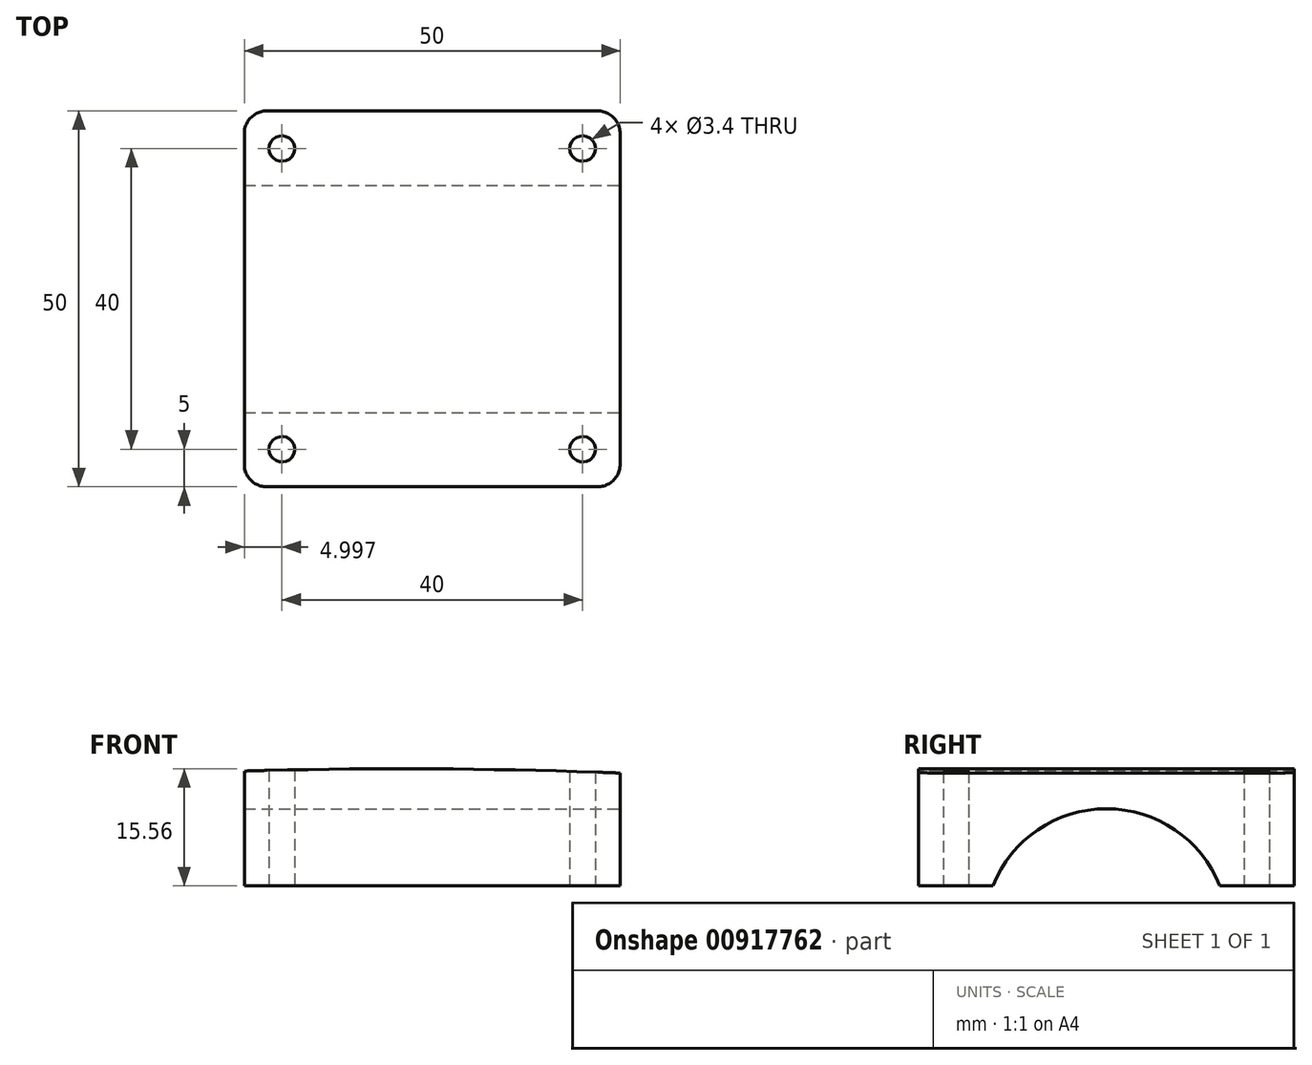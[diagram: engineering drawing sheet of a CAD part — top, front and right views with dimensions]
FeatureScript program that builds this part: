
annotation { "Feature Type Name" : "Feature", "Feature Type Description" : "" }
export const myFeature = defineFeature(function(context is Context, id is Id, definition is map)
    precondition{}
    {
        {
            var Q0;
            Q0=qCreatedBy(makeId("Front.planeOp"),FACE);
            var sketch = newSketch(context, id + "F0", { "sketchPlane" : qUnion([Q0])});
            skLineSegment(sketch, "E0.bottom", {"start": v(28.73, 9.53) * mm, "end": v(-21.27, 9.53) * mm});
            skLineSegment(sketch, "E0.left", {"start": v(28.73, 9.53) * mm, "end": v(28.73, 24.53) * mm});
            skLineSegment(sketch, "E0.right", {"start": v(-21.27, 9.53) * mm, "end": v(-21.27, 24.8) * mm});
            skArc(sketch, "E1", {"start": v(28.73, 24.53) * mm, "mid": v(3.73, 25.08) * mm, "end": v(-21.27, 24.8) * mm});
            skSolve(sketch);
        }
        {
            var Q0;
            Q0 = qSketchRegion(id + "F0", true);
            extrude(context, id + "F1", {"entities" : qUnion([Q0]), "depth" : 50 * mm, "offsetDistance" : 25 * mm});
        }
        {
            var Q0;
            Q0=makeQuery(id+"F1.opExtrude","SWEPT_FACE",FACE,{"disambiguationData":[OSD([sQuery(id+"F0.wireOp",EDGE,"E0.left")])]});
            var sketch = newSketch(context, id + "F2", { "sketchPlane" : qUnion([Q0])});
            skCircle(sketch, "E2", {"center": v(-25, 3.53) * mm, "radius": 16.25 * mm});
            skSolve(sketch);
        }
        {
            var Q0;
            Q0 = qSketchRegion(id + "F2", true);
            extrude(context, id + "F3", {"entities" : qUnion([Q0]), "operationType" : NewBodyOperationType.REMOVE, "endBound" : BoundingType.THROUGH_ALL, "oppositeDirection" : true, "depth" : 25 * mm, "offsetDistance" : 25 * mm});
        }
        {
            var Q0;
            {var subQ0=sQuery(id+"F0.wireOp",EDGE,"E0.right");var subQ1=sQuery(id+"F0.wireOp",EDGE,"E0.left");var subQ2=sQuery(id+"F0.wireOp",EDGE,"E0.bottom");Q0=makeQuery(id+"F3.boolean.opBoolean","SPLIT",FACE,{"disambiguationData":[TD([makeQuery(id+"F1.opExtrude","CAP_FACE",FACE,{"disambiguationData":[OSD([subQ2,subQ1,subQ0,sQuery(id+"F0.wireOp",EDGE,"E1")])],"isStart":false})])],"derivedFrom":makeQuery(id+"F1.opExtrude","SWEPT_FACE",FACE,{"disambiguationData":[OSD([subQ2])]})});}
            var sketch = newSketch(context, id + "F4", { "sketchPlane" : qUnion([Q0])});
            skPoint(sketch, "E3", {"position": v(-16.27, 45) * mm});
            skPoint(sketch, "E4", {"position": v(23.73, 45) * mm});
            skPoint(sketch, "E5", {"position": v(23.73, 5) * mm});
            skPoint(sketch, "E6", {"position": v(-16.27, 5) * mm});
            skCircle(sketch, "E7", {"center": v(-16.27, 45) * mm, "radius": 1.7 * mm});
            skCircle(sketch, "E8", {"center": v(23.73, 45) * mm, "radius": 1.7 * mm});
            skCircle(sketch, "E9", {"center": v(-16.27, 5) * mm, "radius": 1.7 * mm});
            skCircle(sketch, "E10", {"center": v(23.73, 5) * mm, "radius": 1.7 * mm});
            skSolve(sketch);
        }
        {
            var Q0;
            Q0 = qSketchRegion(id + "F4", true);
            extrude(context, id + "F5", {"entities" : qUnion([Q0]), "operationType" : NewBodyOperationType.REMOVE, "endBound" : BoundingType.THROUGH_ALL, "oppositeDirection" : true, "depth" : 25 * mm, "offsetDistance" : 25 * mm});
        }
        {
            var Q0;
            Q0=makeQuery(id+"F1.opExtrude","CAP_EDGE",EDGE,{"disambiguationData":[OSD([sQuery(id+"F0.wireOp",EDGE,"E0.left")])],"isStart":false});
            var Q1;
            Q1=makeQuery(id+"F1.opExtrude","CAP_EDGE",EDGE,{"disambiguationData":[OSD([sQuery(id+"F0.wireOp",EDGE,"E0.right")])],"isStart":false});
            var Q2;
            Q2=makeQuery(id+"F1.opExtrude","CAP_EDGE",EDGE,{"disambiguationData":[OSD([sQuery(id+"F0.wireOp",EDGE,"E0.right")])],"isStart":true});
            var Q3;
            Q3=makeQuery(id+"F1.opExtrude","CAP_EDGE",EDGE,{"disambiguationData":[OSD([sQuery(id+"F0.wireOp",EDGE,"E0.left")])],"isStart":true});
            fillet(context, id + "F6", {"entities" : qUnion([Q0, Q1, Q2, Q3]), "radius" : 3 * mm, "tangentPropagation" : true, "allowEdgeOverflow" : false});
        }
    });
